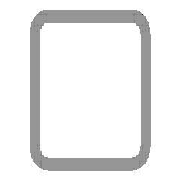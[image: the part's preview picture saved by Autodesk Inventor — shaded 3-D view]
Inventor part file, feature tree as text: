
AUTODESK INVENTOR PART (.ipt)
format: ipt  version: 2021 (Build 250183000, 183)  size: 150,528 bytes
history: native  units: mm (DEFAULTED — no unit token found)
features: other x6, sketch x3, split x2, extrude x1, plane x1
ambient origin geometry x8: Origin, YZ Plane, XZ Plane, XY Plane, X Axis, Y Axis, Z Axis, Center Point
bodies: Solid1 (feature_tree)
feature tree (13):
  parser-record x1  (decoder bookkeeping rows leaked as tree rows — omitted from the tree; the rows remain in map.json)
  other  "Driven Length"
  other  "Plano inicial"
  other  "Plano final"
  extrude  "Corpo"  TaperAngle=0.0deg  [1 undecoded]
  other  "Plano de trabalho4"
  split  "Dividir1"
  other  "Plano de trabalho5"
  split  "Dividir2"
  sketch  "Esboço"  dims[d11=50.8mm d12=4.7625mm d13=-25.4mm d14=4025.4mm d15=25.4mm d16=25.4mm d17=9.525mm d18=90.0deg d19=4050.8mm]
  sketch  "Sketch3"  dims[d3=4050.8mm d4=0.0mm]
  plane  "Work Plane3"
  sketch  "Sketch4"  dims[d10=50.8mm]
note: 1 required parameter value undecoded (feature->parameter linkage not recoverable at this tier; creation-order binding heuristic only, values carry confidence <= 0.55)
